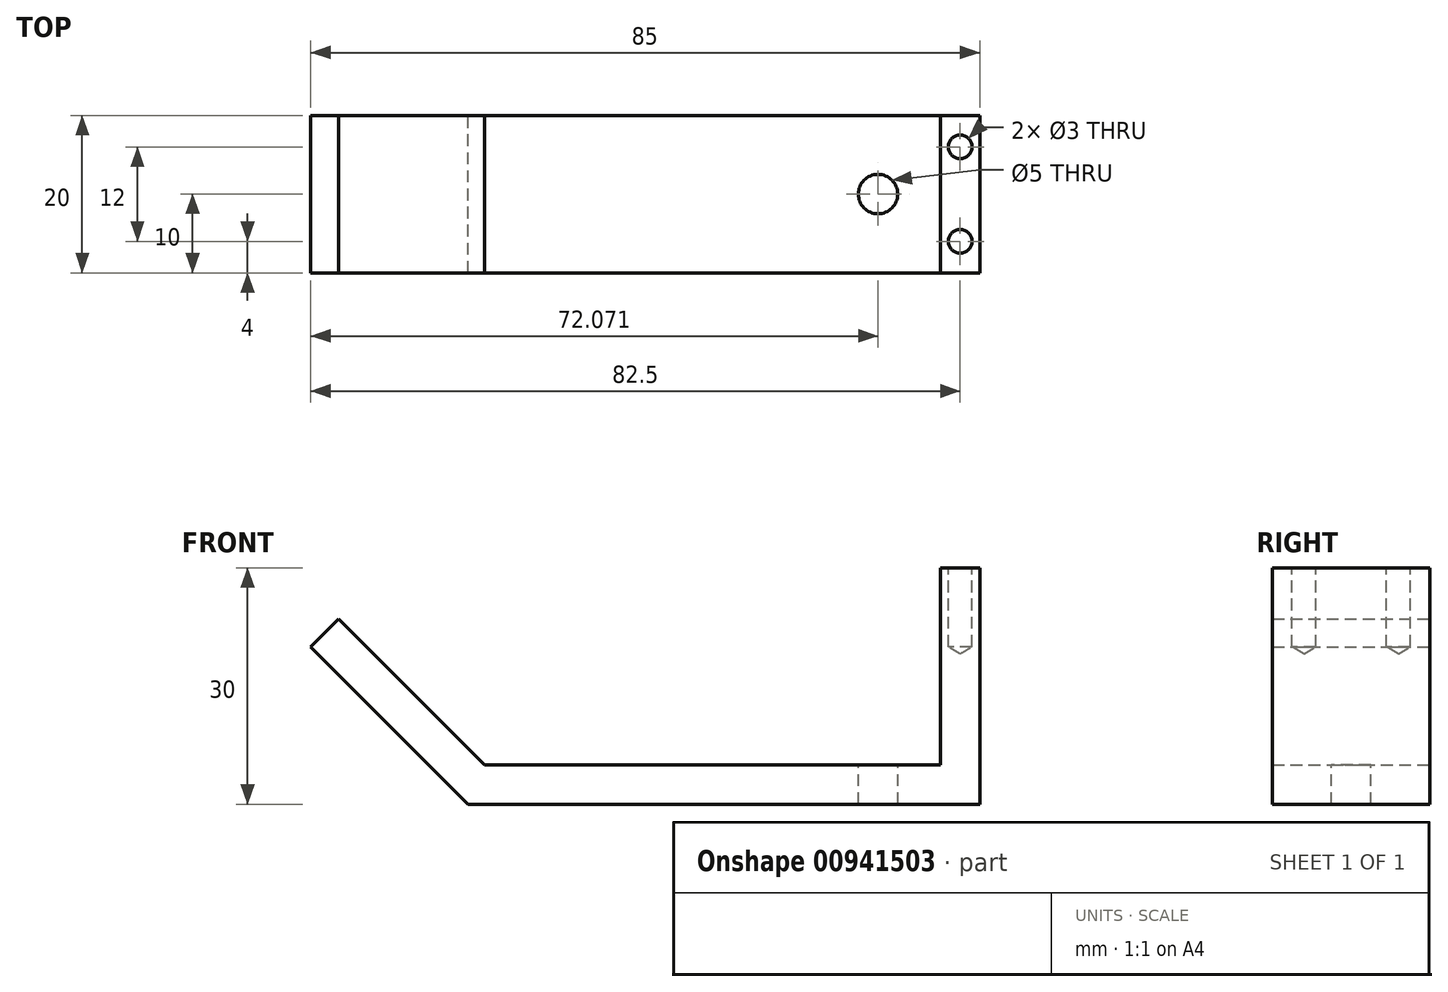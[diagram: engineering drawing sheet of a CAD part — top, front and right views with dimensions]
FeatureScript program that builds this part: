
annotation { "Feature Type Name" : "Feature", "Feature Type Description" : "" }
export const myFeature = defineFeature(function(context is Context, id is Id, definition is map)
    precondition{}
    {
        {
            var Q0;
            Q0=qCreatedBy(makeId("Front.planeOp"),FACE);
            var sketch = newSketch(context, id + "F0", { "sketchPlane" : qUnion([Q0])});
            skLineSegment(sketch, "E0", {"start": v(0, 0) * mm, "end": v(-65, 0) * mm});
            skLineSegment(sketch, "E1", {"start": v(-65, 0) * mm, "end": v(-85, 20) * mm});
            skLineSegment(sketch, "E2", {"start": v(-85, 20) * mm, "end": v(-81.46, 23.54) * mm});
            skLineSegment(sketch, "E3", {"start": v(-81.46, 23.54) * mm, "end": v(-62.93, 5) * mm});
            skLineSegment(sketch, "E4", {"start": v(-62.93, 5) * mm, "end": v(0, 5) * mm});
            skLineSegment(sketch, "E5", {"start": v(0, 5) * mm, "end": v(0, 0) * mm});
            skLineSegment(sketch, "E6", {"start": v(-62.93, -5.14) * mm, "end": v(-62.93, 21.92) * mm, "construction": true});
            skSolve(sketch);
        }
        {
            var Q0;
            Q0 = qSketchRegion(id + "F0", true);
            extrude(context, id + "F1", {"entities" : qUnion([Q0]), "depth" : 20 * mm, "offsetDistance" : 25 * mm});
        }
        {
            var Q0;
            Q0=makeQuery(id+"F1.opExtrude","SWEPT_FACE",FACE,{"disambiguationData":[OSD([sQuery(id+"F0.wireOp",EDGE,"E3")])]});
            var sketch = newSketch(context, id + "F2", { "sketchPlane" : qUnion([Q0])});
            skCircle(sketch, "E7", {"center": v(-70.25, -10) * mm, "radius": 2.6 * mm});
            skPoint(sketch, "E7.centerSnap0", {"position": v(-74.25, -10) * mm});
            skSolve(sketch);
        }
        {
            var Q0;
            Q0=makeQuery(id+"F2.imprint","IMPRINT",FACE,{"disambiguationData":[TD([[makeQuery(id+"F2.imprint","IMPRINT",EDGE,{"derivedFrom":sQuery(id+"F2.wireOp",EDGE,"E7")}),1.0]])]});
            extrude(context, id + "F3", {"entities" : qUnion([Q0]), "operationType" : NewBodyOperationType.REMOVE, "endBound" : BoundingType.THROUGH_ALL, "oppositeDirection" : true, "depth" : 25 * mm, "offsetDistance" : 25 * mm});
        }
        {
            var Q0;
            Q0=makeQuery(id+"F1.opExtrude","SWEPT_FACE",FACE,{"disambiguationData":[OSD([sQuery(id+"F0.wireOp",EDGE,"E4")])]});
            var sketch = newSketch(context, id + "F4", { "sketchPlane" : qUnion([Q0])});
            skCircle(sketch, "E8", {"center": v(-12.93, -10) * mm, "radius": 2.5 * mm});
            skPoint(sketch, "E8.centerSnap0", {"position": v(-12.93, -20) * mm});
            skPoint(sketch, "E8.centerSnap1", {"position": v(0, -10) * mm});
            skSolve(sketch);
        }
        {
            var Q0;
            Q0=makeQuery(id+"F4.imprint","IMPRINT",FACE,{"disambiguationData":[TD([[makeQuery(id+"F4.imprint","IMPRINT",EDGE,{"derivedFrom":sQuery(id+"F4.wireOp",EDGE,"E8")}),1.0]])]});
            extrude(context, id + "F5", {"entities" : qUnion([Q0]), "operationType" : NewBodyOperationType.REMOVE, "endBound" : BoundingType.THROUGH_ALL, "oppositeDirection" : true, "depth" : 25 * mm, "offsetDistance" : 25 * mm});
        }
        {
            var Q0;
            Q0=makeQuery(id+"F1.opExtrude","SWEPT_FACE",FACE,{"disambiguationData":[OSD([sQuery(id+"F0.wireOp",EDGE,"E3")])]});
            var sketch = newSketch(context, id + "F6", { "sketchPlane" : qUnion([Q0])});
            skCircle(sketch, "E9", {"center": v(-70.25, -10) * mm, "radius": 3.05 * mm});
            skSolve(sketch);
        }
        {
            var Q0;
            Q0 = qSketchRegion(id + "F6", true);
            extrude(context, id + "F7", {"entities" : qUnion([Q0]), "operationType" : NewBodyOperationType.REMOVE, "oppositeDirection" : true, "depth" : 2 * mm, "offsetDistance" : 25 * mm});
        }
        {
            var Q0;
            Q0=makeQuery(id+"F1.opExtrude","SWEPT_FACE",FACE,{"disambiguationData":[OSD([sQuery(id+"F0.wireOp",EDGE,"E4")])]});
            var sketch = newSketch(context, id + "F8", { "sketchPlane" : qUnion([Q0])});
            skLineSegment(sketch, "E10.bottom", {"start": v(0, -20) * mm, "end": v(-5, -20) * mm});
            skLineSegment(sketch, "E10.top", {"start": v(0, 0) * mm, "end": v(-5, 0) * mm});
            skLineSegment(sketch, "E10.left", {"start": v(0, -20) * mm, "end": v(0, 0) * mm});
            skLineSegment(sketch, "E10.right", {"start": v(-5, -20) * mm, "end": v(-5, 0) * mm});
            skSolve(sketch);
        }
        {
            var Q0;
            Q0=makeQuery(id+"F8.imprint","IMPRINT",FACE,{"disambiguationData":[TD([[makeQuery(id+"F8.imprint","IMPRINT",EDGE,{"derivedFrom":sQuery(id+"F8.wireOp",EDGE,"E10.bottom")}),1.0]])]});
            extrude(context, id + "F9", {"entities" : qUnion([Q0]), "operationType" : NewBodyOperationType.ADD, "depth" : 25 * mm, "offsetDistance" : 25 * mm});
        }
        {
            var Q0;
            Q0=makeQuery(id+"F9.opExtrude","CAP_FACE",FACE,{"disambiguationData":[OSD([sQuery(id+"F8.wireOp",EDGE,"E10.bottom"),sQuery(id+"F8.wireOp",EDGE,"E10.top"),sQuery(id+"F8.wireOp",EDGE,"E10.left"),sQuery(id+"F8.wireOp",EDGE,"E10.right")])],"isStart":false});
            var sketch = newSketch(context, id + "F10", { "sketchPlane" : qUnion([Q0])});
            skPoint(sketch, "E11", {"position": v(-2.5, -16) * mm});
            skPoint(sketch, "E11.positionSnap0", {"position": v(-2.5, -20) * mm});
            skPoint(sketch, "E12", {"position": v(-2.5, -4) * mm});
            skPoint(sketch, "E12.positionSnap0", {"position": v(-2.5, 0) * mm});
            skLineSegment(sketch, "E13", {"start": v(-5, -10) * mm, "end": v(0, -10) * mm, "construction": true});
            skSolve(sketch);
        }
        {
            var Q0;
            Q0=sQuery(id+"F10.wireOp",VERTEX,"E11");
            var Q1;
            Q1=sQuery(id+"F10.wireOp",VERTEX,"E12");
            var Q2;
            Q2=makeQuery(id+"F1.opExtrude","SWEPT_BODY",BODY,{"disambiguationData":[OSD([sQuery(id+"F0.wireOp",EDGE,"E0"),sQuery(id+"F0.wireOp",EDGE,"E1"),sQuery(id+"F0.wireOp",EDGE,"E2"),sQuery(id+"F0.wireOp",EDGE,"E3"),sQuery(id+"F0.wireOp",EDGE,"E4"),sQuery(id+"F0.wireOp",EDGE,"E5")])]});
            hole(context, id + "F11", {"style" : HoleStyle.SIMPLE, "endStyle" : HoleEndStyle.BLIND, "holeDiameter" : 3 * mm, "majorDiameter" : 5 * mm, "holeDepth" : 10 * mm, "isTappedThrough" : true, "tappedDepth" : 12 * mm, "tapClearance" : 3, "startFromSketch" : true, "locations" : qUnion([Q0, Q1]), "scope" : qUnion([Q2])});
        }
    });
